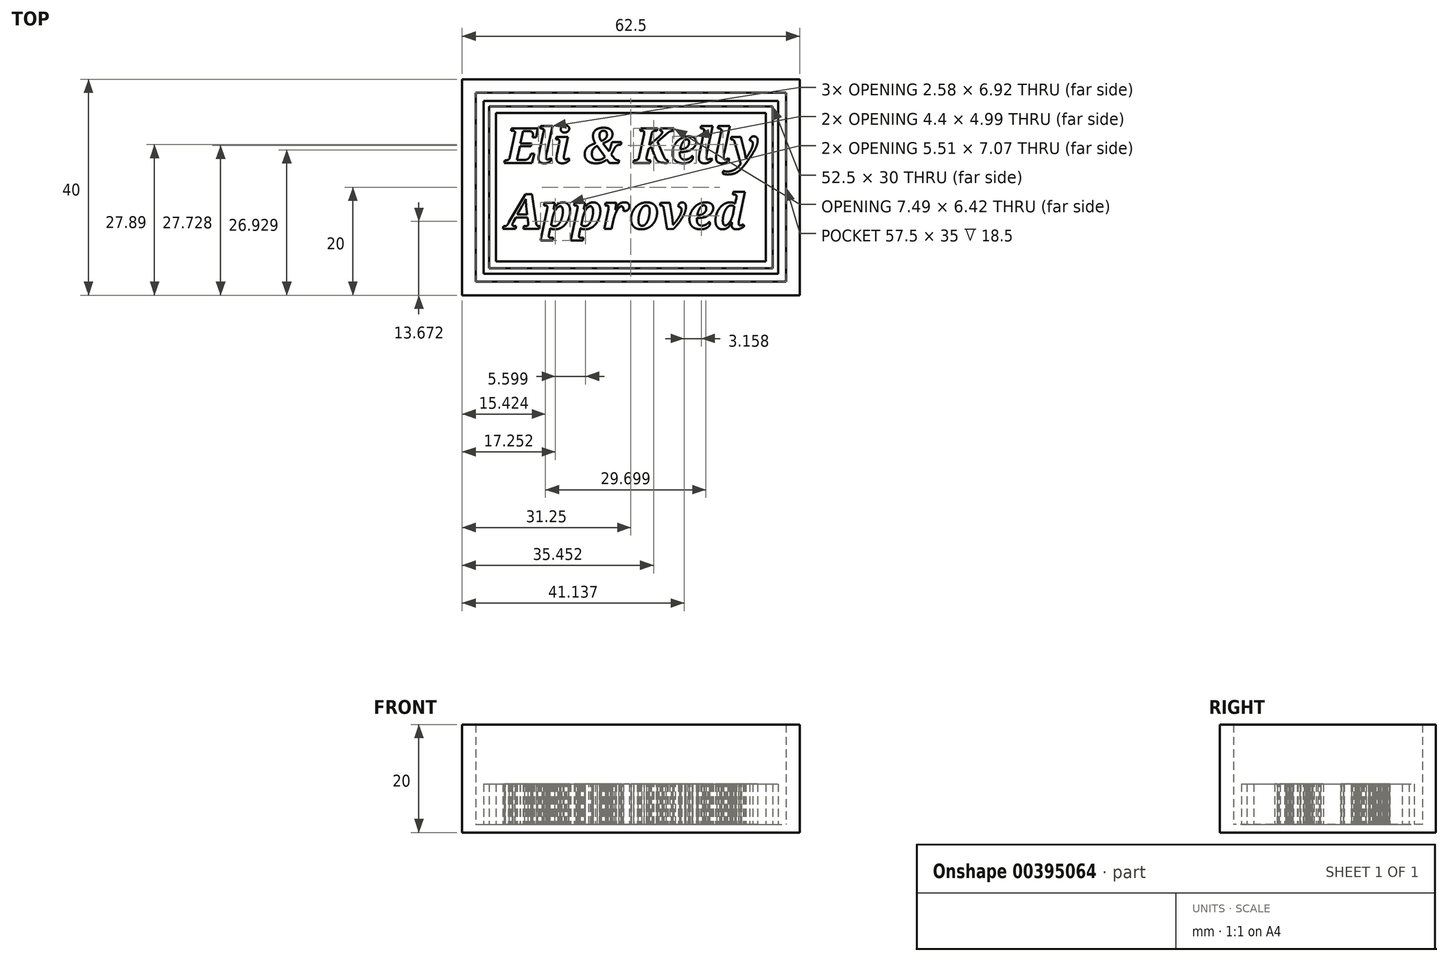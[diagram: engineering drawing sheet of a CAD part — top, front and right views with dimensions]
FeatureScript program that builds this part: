
annotation { "Feature Type Name" : "Feature", "Feature Type Description" : "" }
export const myFeature = defineFeature(function(context is Context, id is Id, definition is map)
    precondition{}
    {
        {
            var Q0;
            Q0=qCreatedBy(makeId("Top.planeOp"),FACE);
            var sketch = newSketch(context, id + "F0", { "sketchPlane" : qUnion([Q0])});
            skLineSegment(sketch, "E0.bottom", {"start": v(-28.75, -17.5) * mm, "end": v(28.75, -17.5) * mm, "construction": true});
            skLineSegment(sketch, "E0.top", {"start": v(-28.75, 17.5) * mm, "end": v(28.75, 17.5) * mm, "construction": true});
            skLineSegment(sketch, "E0.left", {"start": v(-28.75, -17.5) * mm, "end": v(-28.75, 17.5) * mm, "construction": true});
            skLineSegment(sketch, "E0.right", {"start": v(28.75, -17.5) * mm, "end": v(28.75, 17.5) * mm, "construction": true});
            skPoint(sketch, "E0.middle", {"position": v(0, 0) * mm});
            skLineSegment(sketch, "E1.bottom", {"start": v(-25, -13.75) * mm, "end": v(25, -13.75) * mm});
            skLineSegment(sketch, "E1.top", {"start": v(-25, 13.75) * mm, "end": v(25, 13.75) * mm});
            skLineSegment(sketch, "E1.left", {"start": v(-25, -13.75) * mm, "end": v(-25, 13.75) * mm});
            skLineSegment(sketch, "E2", {"start": v(25, 13.75) * mm, "end": v(25, -13.75) * mm});
            skText(sketch, "E3", { "text": "Eli & Kelly\nApproved", "fontName": "NotoSerif-BoldItalic.ttf"});
            skLineSegment(sketch, "E4.bottom", {"start": v(-27.25, -16) * mm, "end": v(27.25, -16) * mm});
            skLineSegment(sketch, "E4.top", {"start": v(-27.25, 16) * mm, "end": v(27.25, 16) * mm});
            skLineSegment(sketch, "E4.left", {"start": v(-27.25, -16) * mm, "end": v(-27.25, 16) * mm});
            skLineSegment(sketch, "E4.right", {"start": v(27.25, -16) * mm, "end": v(27.25, 16) * mm});
            skLineSegment(sketch, "E5.bottom", {"start": v(-26.25, -15) * mm, "end": v(26.25, -15) * mm});
            skLineSegment(sketch, "E5.top", {"start": v(-26.25, 15) * mm, "end": v(26.25, 15) * mm});
            skLineSegment(sketch, "E5.left", {"start": v(-26.25, -15) * mm, "end": v(-26.25, 15) * mm});
            skLineSegment(sketch, "E5.right", {"start": v(26.25, -15) * mm, "end": v(26.25, 15) * mm});
            const initialGuessF0  = {"E3": [-0.02325, 0.00452, 1, 0, 0.00647]};
            skSetInitialGuess(sketch, initialGuessF0);
            skSolve(sketch);
        }
        {
            var Q0;
            Q0=makeQuery(id+"F0.imprint","IMPRINT",FACE,{"disambiguationData":[TD([[makeQuery(id+"F0.imprint","IMPRINT",EDGE,{"derivedFrom":sQuery(id+"F0.wireOp",EDGE,"E1.bottom")}),1.0]])]});
            var Q1;
            Q1=makeQuery(id+"F0.imprint","IMPRINT",FACE,{"disambiguationData":[TD([[makeQuery(id+"F0.imprint","IMPRINT",EDGE,{"derivedFrom":sQuery(id+"F0.wireOp",EDGE,"E3.sketch_text.stroke-156")}),1.0]])]});
            var Q2;
            Q2=makeQuery(id+"F0.imprint","IMPRINT",FACE,{"disambiguationData":[TD([[makeQuery(id+"F0.imprint","IMPRINT",EDGE,{"derivedFrom":sQuery(id+"F0.wireOp",EDGE,"E3.sketch_text.stroke-167")}),1.0]])]});
            var Q3;
            Q3=makeQuery(id+"F0.imprint","IMPRINT",FACE,{"disambiguationData":[TD([[makeQuery(id+"F0.imprint","IMPRINT",EDGE,{"derivedFrom":sQuery(id+"F0.wireOp",EDGE,"E3.sketch_text.stroke-272")}),1.0]])]});
            var Q4;
            Q4=makeQuery(id+"F0.imprint","IMPRINT",FACE,{"disambiguationData":[TD([[makeQuery(id+"F0.imprint","IMPRINT",EDGE,{"derivedFrom":sQuery(id+"F0.wireOp",EDGE,"E3.sketch_text.stroke-412")}),1.0]])]});
            var Q5;
            Q5=makeQuery(id+"F0.imprint","IMPRINT",FACE,{"disambiguationData":[TD([[makeQuery(id+"F0.imprint","IMPRINT",EDGE,{"derivedFrom":sQuery(id+"F0.wireOp",EDGE,"E3.sketch_text.stroke-423")}),1.0]])]});
            var Q6;
            Q6=makeQuery(id+"F0.imprint","IMPRINT",FACE,{"disambiguationData":[TD([[makeQuery(id+"F0.imprint","IMPRINT",EDGE,{"derivedFrom":sQuery(id+"F0.wireOp",EDGE,"E3.sketch_text.stroke-489")}),1.0]])]});
            var Q7;
            Q7=makeQuery(id+"F0.imprint","IMPRINT",FACE,{"disambiguationData":[TD([[makeQuery(id+"F0.imprint","IMPRINT",EDGE,{"derivedFrom":sQuery(id+"F0.wireOp",EDGE,"E3.sketch_text.stroke-605")}),1.0]])]});
            var Q8;
            Q8=makeQuery(id+"F0.imprint","IMPRINT",FACE,{"disambiguationData":[TD([[makeQuery(id+"F0.imprint","IMPRINT",EDGE,{"derivedFrom":sQuery(id+"F0.wireOp",EDGE,"E3.sketch_text.stroke-684")}),1.0]])]});
            var Q9;
            Q9=makeQuery(id+"F0.imprint","IMPRINT",FACE,{"disambiguationData":[TD([[makeQuery(id+"F0.imprint","IMPRINT",EDGE,{"derivedFrom":sQuery(id+"F0.wireOp",EDGE,"E3.sketch_text.stroke-695")}),1.0]])]});
            var Q10;
            Q10=makeQuery(id+"F0.imprint","IMPRINT",FACE,{"disambiguationData":[TD([[makeQuery(id+"F0.imprint","IMPRINT",EDGE,{"derivedFrom":sQuery(id+"F0.wireOp",EDGE,"E4.bottom")}),1.0]])]});
            extrude(context, id + "F1", {"entities" : qUnion([Q0, Q1, Q2, Q3, Q4, Q5, Q6, Q7, Q8, Q9, Q10]), "depth" : 7.5 * mm});
        }
        {
            var Q0;
            Q0=makeQuery(id+"F1.opExtrude","CAP_FACE",FACE,{"disambiguationData":[OSD([sQuery(id+"F0.wireOp",EDGE,"E4.bottom"),sQuery(id+"F0.wireOp",EDGE,"E4.top"),sQuery(id+"F0.wireOp",EDGE,"E4.left"),sQuery(id+"F0.wireOp",EDGE,"E4.right"),sQuery(id+"F0.wireOp",EDGE,"E5.bottom"),sQuery(id+"F0.wireOp",EDGE,"E5.top"),sQuery(id+"F0.wireOp",EDGE,"E5.left"),sQuery(id+"F0.wireOp",EDGE,"E5.right")])],"isStart":true});
            var sketch = newSketch(context, id + "F2", { "sketchPlane" : qUnion([Q0])});
            skLineSegment(sketch, "E6.bottom", {"start": v(-28.75, -17.5) * mm, "end": v(28.75, -17.5) * mm});
            skLineSegment(sketch, "E6.top", {"start": v(-28.75, 17.5) * mm, "end": v(28.75, 17.5) * mm});
            skLineSegment(sketch, "E6.left", {"start": v(-28.75, -17.5) * mm, "end": v(-28.75, 17.5) * mm});
            skLineSegment(sketch, "E6.right", {"start": v(28.75, -17.5) * mm, "end": v(28.75, 17.5) * mm});
            skPoint(sketch, "E6.middle", {"position": v(0, 0) * mm});
            skSolve(sketch);
        }
        {
            var Q0;
            Q0 = qSketchRegion(id + "F2", true);
            extrude(context, id + "F3", {"entities" : qUnion([Q0]), "depth" : 1.5 * mm});
        }
        {
            var Q0;
            Q0=makeQuery(id+"F3.opExtrude","CAP_FACE",FACE,{"disambiguationData":[OSD([sQuery(id+"F2.wireOp",EDGE,"E6.bottom"),sQuery(id+"F2.wireOp",EDGE,"E6.top"),sQuery(id+"F2.wireOp",EDGE,"E6.left"),sQuery(id+"F2.wireOp",EDGE,"E6.right")])],"isStart":false});
            var sketch = newSketch(context, id + "F4", { "sketchPlane" : qUnion([Q0])});
            skLineSegment(sketch, "E7.bottom", {"start": v(-31.25, -20) * mm, "end": v(31.25, -20) * mm});
            skLineSegment(sketch, "E7.top", {"start": v(-31.25, 20) * mm, "end": v(31.25, 20) * mm});
            skLineSegment(sketch, "E7.left", {"start": v(-31.25, -20) * mm, "end": v(-31.25, 20) * mm});
            skLineSegment(sketch, "E7.right", {"start": v(31.25, -20) * mm, "end": v(31.25, 20) * mm});
            skPoint(sketch, "E7.middle", {"position": v(0, 0) * mm});
            skLineSegment(sketch, "E8.bottom", {"start": v(-28.75, -17.5) * mm, "end": v(28.75, -17.5) * mm});
            skLineSegment(sketch, "E8.top", {"start": v(-28.75, 17.5) * mm, "end": v(28.75, 17.5) * mm});
            skLineSegment(sketch, "E8.left", {"start": v(-28.75, -17.5) * mm, "end": v(-28.75, 17.5) * mm});
            skLineSegment(sketch, "E8.right", {"start": v(28.75, -17.5) * mm, "end": v(28.75, 17.5) * mm});
            skSolve(sketch);
        }
        {
            var Q0;
            Q0 = qSketchRegion(id + "F4", true);
            extrude(context, id + "F5", {"entities" : qUnion([Q0]), "operationType" : NewBodyOperationType.ADD, "oppositeDirection" : true, "depth" : 20 * mm});
        }
    });
